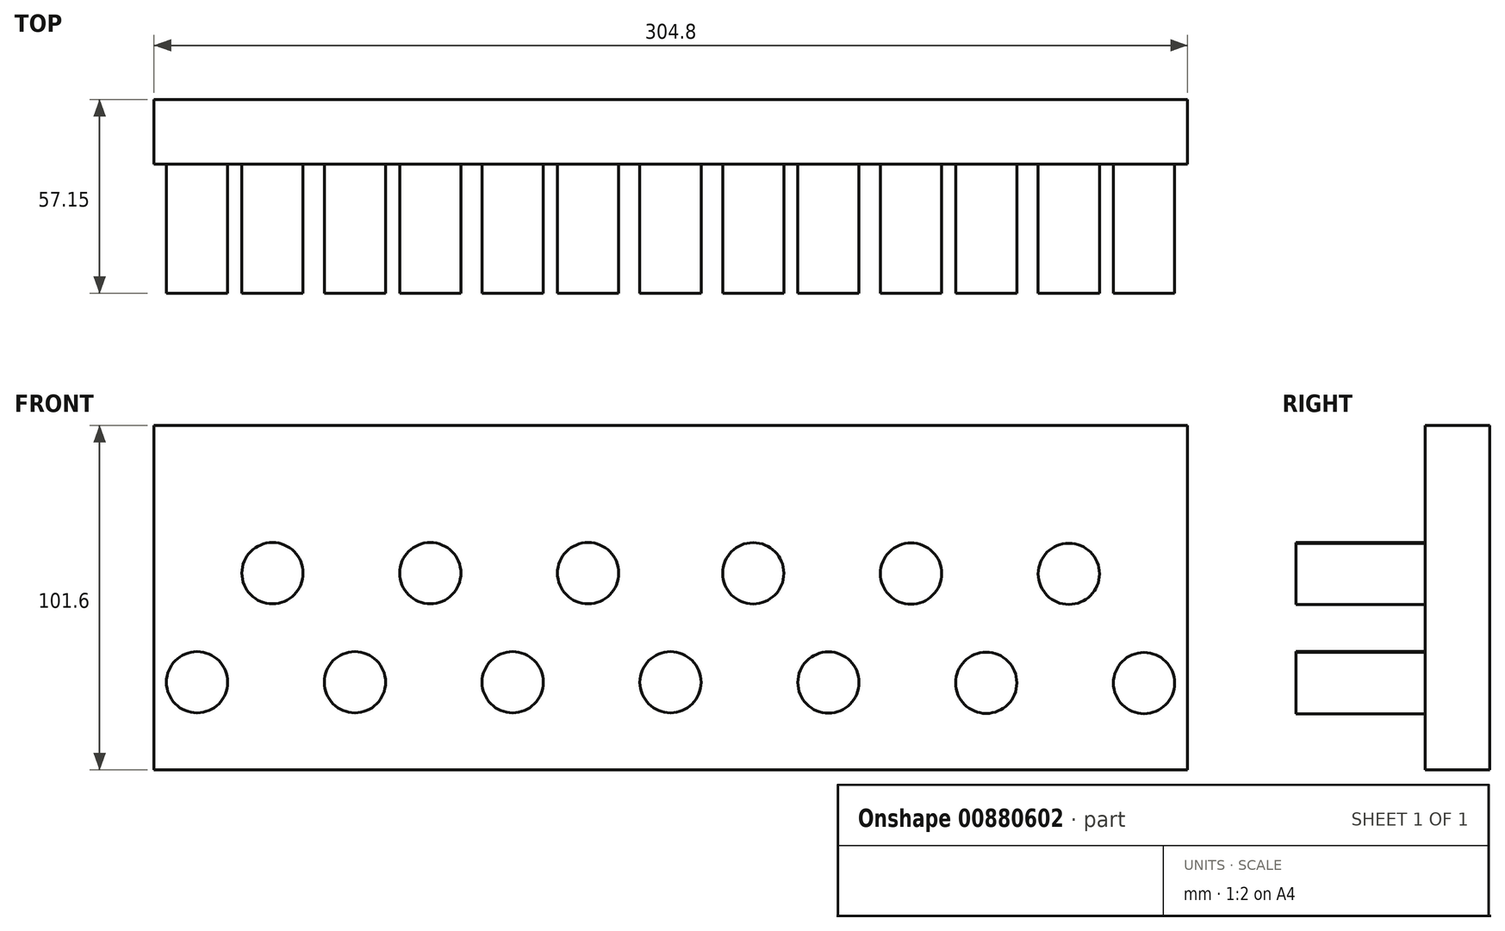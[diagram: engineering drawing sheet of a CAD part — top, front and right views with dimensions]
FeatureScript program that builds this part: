
annotation { "Feature Type Name" : "Feature", "Feature Type Description" : "" }
export const myFeature = defineFeature(function(context is Context, id is Id, definition is map)
    precondition{}
    {
        {
            var Q0;
            Q0=qCreatedBy(makeId("Front.planeOp"),FACE);
            var sketch = newSketch(context, id + "F0", { "sketchPlane" : qUnion([Q0])});
            skLineSegment(sketch, "E0.bottom", {"start": v(152.4, -50.8) * mm, "end": v(-152.4, -50.8) * mm});
            skLineSegment(sketch, "E0.top", {"start": v(152.4, 50.8) * mm, "end": v(-152.4, 50.8) * mm});
            skLineSegment(sketch, "E0.left", {"start": v(152.4, -50.8) * mm, "end": v(152.4, 50.8) * mm});
            skLineSegment(sketch, "E0.right", {"start": v(-152.4, -50.8) * mm, "end": v(-152.4, 50.8) * mm});
            skPoint(sketch, "E0.middle", {"position": v(0, 0) * mm});
            skSolve(sketch);
        }
        {
            var Q0;
            Q0=makeQuery(id+"F0.imprint","IMPRINT",FACE,{"disambiguationData":[TD([[makeQuery(id+"F0.imprint","IMPRINT",EDGE,{"derivedFrom":sQuery(id+"F0.wireOp",EDGE,"E0.bottom")}),-1.0]])]});
            extrude(context, id + "F1", {"entities" : qUnion([Q0]), "oppositeDirection" : true, "depth" : 19.05 * mm, "offsetDistance" : 25.4 * mm});
        }
        {
            var Q0;
            Q0=makeQuery(id+"F1.opExtrude","CAP_FACE",FACE,{"disambiguationData":[OSD([sQuery(id+"F0.wireOp",EDGE,"E0.bottom"),sQuery(id+"F0.wireOp",EDGE,"E0.top"),sQuery(id+"F0.wireOp",EDGE,"E0.left"),sQuery(id+"F0.wireOp",EDGE,"E0.right")])],"isStart":true});
            var sketch = newSketch(context, id + "F2", { "sketchPlane" : qUnion([Q0])});
            skCircle(sketch, "E1", {"center": v(-93.16, -24.95) * mm, "radius": 9.03 * mm});
            skPoint(sketch, "E2", {"position": v(-152.4, 0) * mm});
            skCircle(sketch, "E3", {"center": v(-139.7, -24.95) * mm, "radius": 9.03 * mm});
            skCircle(sketch, "E4", {"center": v(-117.47, 7.24) * mm, "radius": 9.03 * mm});
            skCircle(sketch, "E5", {"center": v(-70.93, 7.24) * mm, "radius": 9.03 * mm});
            skCircle(sketch, "E6", {"center": v(-46.62, -24.95) * mm, "radius": 9.03 * mm});
            skCircle(sketch, "E7", {"center": v(-24.38, 7.24) * mm, "radius": 9.03 * mm});
            skCircle(sketch, "E8", {"center": v(-0.1, -24.95) * mm, "radius": 9.03 * mm});
            skCircle(sketch, "E9.MirrorC", {"center": v(70.85, 7.1) * mm, "radius": 9.03 * mm});
            skCircle(sketch, "E10.MirrorC", {"center": v(139.56, -25.2) * mm, "radius": 9.03 * mm});
            skCircle(sketch, "E11.MirrorC", {"center": v(46.49, -25.03) * mm, "radius": 9.03 * mm});
            skCircle(sketch, "E12.MirrorC", {"center": v(24.3, 7.2) * mm, "radius": 9.03 * mm});
            skCircle(sketch, "E13.MirrorC", {"center": v(117.4, 7.03) * mm, "radius": 9.03 * mm});
            skCircle(sketch, "E14.MirrorC", {"center": v(93.02, -25.12) * mm, "radius": 9.03 * mm});
            skSolve(sketch);
        }
        {
            var Q0;
            Q0 = qSketchRegion(id + "F2", true);
            extrude(context, id + "F3", {"entities" : qUnion([Q0]), "operationType" : NewBodyOperationType.ADD, "depth" : 38.1 * mm, "offsetDistance" : 25.4 * mm});
        }
    });
